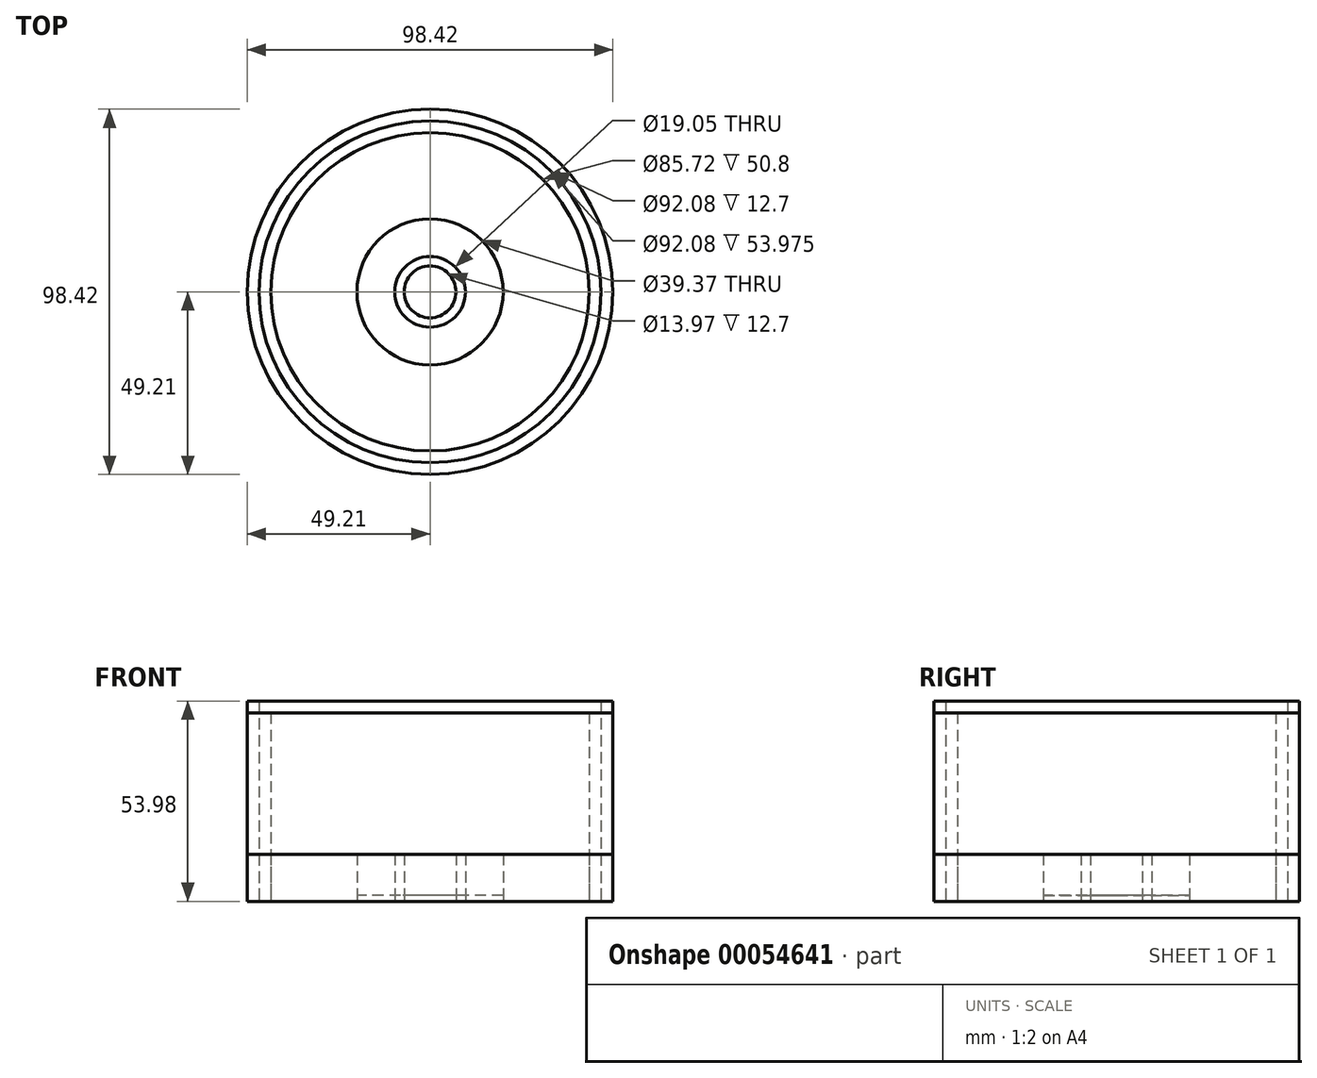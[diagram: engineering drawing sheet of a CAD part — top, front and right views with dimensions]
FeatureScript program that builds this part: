
annotation { "Feature Type Name" : "Feature", "Feature Type Description" : "" }
export const myFeature = defineFeature(function(context is Context, id is Id, definition is map)
    precondition{}
    {
        {
            var Q0;
            Q0=qCreatedBy(makeId("Top.planeOp"),FACE);
            var sketch = newSketch(context, id + "F0", { "sketchPlane" : qUnion([Q0])});
            skCircle(sketch, "E0", {"center": v(0, 0) * mm, "radius": 49.21 * mm});
            skCircle(sketch, "E1", {"center": v(0, 0) * mm, "radius": 46.04 * mm});
            skCircle(sketch, "E2", {"center": v(0, 0) * mm, "radius": 19.69 * mm});
            skCircle(sketch, "E3", {"center": v(0, 0) * mm, "radius": 9.52 * mm});
            skCircle(sketch, "E4", {"center": v(0, 0) * mm, "radius": 6.99 * mm});
            skCircle(sketch, "E5", {"center": v(0, 0) * mm, "radius": 42.86 * mm});
            skSolve(sketch);
        }
        {
            var Q0;
            Q0 = qSketchRegion(id + "F0", true);
            extrude(context, id + "F1", {"entities" : qUnion([Q0]), "depth" : 53.97 * mm});
        }
        {
            var Q0;
            Q0=makeQuery(id+"F0.imprint","IMPRINT",FACE,{"disambiguationData":[TD([[makeQuery(id+"F0.imprint","IMPRINT",EDGE,{"derivedFrom":sQuery(id+"F0.wireOp",EDGE,"E0")}),1.0]])]});
            var Q1;
            Q1=makeQuery(id+"F0.imprint","IMPRINT",FACE,{"disambiguationData":[TD([[makeQuery(id+"F0.imprint","IMPRINT",EDGE,{"derivedFrom":sQuery(id+"F0.wireOp",EDGE,"E1")}),1.0]])]});
            extrude(context, id + "F2", {"entities" : qUnion([Q0, Q1]), "depth" : 50.8 * mm});
        }
        {
            var Q0;
            Q0 = qSketchRegion(id + "F0", true);
            var Q1;
            Q1=makeQuery(id+"F0.imprint","IMPRINT",FACE,{"disambiguationData":[TD([[makeQuery(id+"F0.imprint","IMPRINT",EDGE,{"derivedFrom":sQuery(id+"F0.wireOp",EDGE,"E2")}),-1.0]])]});
            var Q2;
            Q2=makeQuery(id+"F0.imprint","IMPRINT",FACE,{"disambiguationData":[TD([[makeQuery(id+"F0.imprint","IMPRINT",EDGE,{"derivedFrom":sQuery(id+"F0.wireOp",EDGE,"E3")}),1.0]])]});
            extrude(context, id + "F3", {"entities" : qUnion([Q0, Q1, Q2]), "depth" : 12.7 * mm});
        }
        {
            var Q0;
            Q0=makeQuery(id+"F0.imprint","IMPRINT",FACE,{"disambiguationData":[TD([[makeQuery(id+"F0.imprint","IMPRINT",EDGE,{"derivedFrom":sQuery(id+"F0.wireOp",EDGE,"E2")}),1.0]])]});
            var Q1;
            Q1=makeQuery(id+"F0.imprint","IMPRINT",FACE,{"disambiguationData":[TD([[makeQuery(id+"F0.imprint","IMPRINT",EDGE,{"derivedFrom":sQuery(id+"F0.wireOp",EDGE,"E4")}),1.0]])]});
            extrude(context, id + "F4", {"entities" : qUnion([Q0, Q1]), "depth" : 1.59 * mm});
        }
    });
